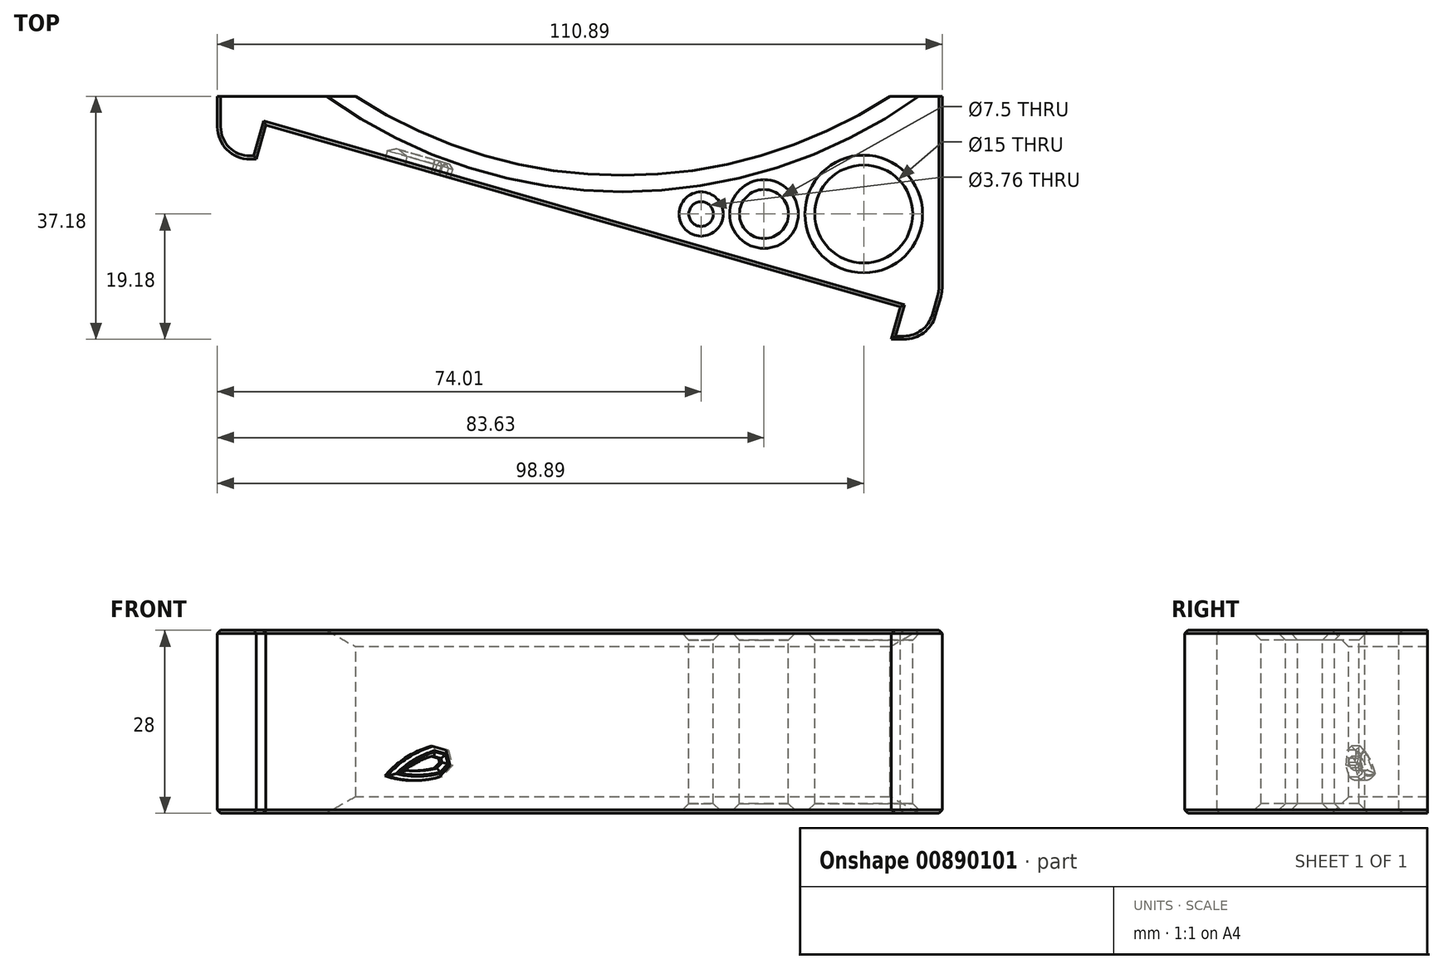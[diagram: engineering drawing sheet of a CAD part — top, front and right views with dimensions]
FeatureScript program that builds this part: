
annotation { "Feature Type Name" : "Feature", "Feature Type Description" : "" }
export const myFeature = defineFeature(function(context is Context, id is Id, definition is map)
    precondition{}
    {
        {
            var Q0;
            Q0=qCreatedBy(makeId("Front.planeOp"),FACE);
            var sketch = newSketch(context, id + "F0", { "sketchPlane" : qUnion([Q0])});
            skLineSegment(sketch, "E0", {"start": v(-54.27, 0) * mm, "end": v(46.5, 0) * mm, "construction": true});
            skLineSegment(sketch, "E1", {"start": v(-54.27, 0) * mm, "end": v(41.86, 27.56) * mm});
            skLineSegment(sketch, "E2", {"start": v(-54.27, 0) * mm, "end": v(-57.03, 9.61) * mm});
            skLineSegment(sketch, "E3", {"start": v(-57.03, 9.61) * mm, "end": v(39.1, 37.18) * mm});
            skLineSegment(sketch, "E4", {"start": v(39.1, 37.18) * mm, "end": v(41.86, 27.56) * mm});
            skSolve(sketch);
        }
        {
            var Q0;
            Q0=makeQuery(id+"F0.imprint","IMPRINT",FACE,{"disambiguationData":[TD([[makeQuery(id+"F0.imprint","IMPRINT",EDGE,{"derivedFrom":sQuery(id+"F0.wireOp",EDGE,"E1")}),1.0]])]});
            extrude(context, id + "F1", {"entities" : qUnion([Q0]), "depth" : 26 * mm, "offsetDistance" : 25 * mm, "symmetric" : true});
        }
        {
            var Q0;
            Q0=qCreatedBy(makeId("Front.planeOp"),FACE);
            var sketch = newSketch(context, id + "F2", { "sketchPlane" : qUnion([Q0])});
            skLineSegment(sketch, "E5.0", {"start": v(-54.61, -0.62) * mm, "end": v(-56.11, 4.61) * mm});
            skLineSegment(sketch, "E5.1", {"start": v(-54.61, -0.62) * mm, "end": v(42.47, 27.22) * mm});
            skLineSegment(sketch, "E5.2", {"start": v(41.05, 32.18) * mm, "end": v(42.47, 27.22) * mm});
            skLineSegment(sketch, "E6", {"start": v(41.05, 32.18) * mm, "end": v(46.77, 32.18) * mm});
            skLineSegment(sketch, "E7", {"start": v(48.86, 24.92) * mm, "end": v(48.86, -5) * mm});
            skLineSegment(sketch, "E8", {"start": v(-56.11, 4.61) * mm, "end": v(-62.03, 4.61) * mm});
            skLineSegment(sketch, "E9", {"start": v(-62.03, 4.61) * mm, "end": v(-62.03, -5) * mm});
            skLineSegment(sketch, "E10", {"start": v(-62.03, -5) * mm, "end": v(-40.86, -5) * mm});
            skLineSegment(sketch, "E11", {"start": v(48.86, 24.92) * mm, "end": v(46.77, 32.18) * mm});
            skArc(sketch, "E12", {"start": v(40.86, -5) * mm, "mid": v(0, 7.1) * mm, "end": v(-40.86, -5) * mm});
            skLineSegment(sketch, "E13.trimOffspring", {"start": v(40.86, -5) * mm, "end": v(48.86, -5) * mm});
            skCircle(sketch, "E14", {"center": v(36.86, 13) * mm, "radius": 7.5 * mm});
            skCircle(sketch, "E15", {"center": v(21.6, 13) * mm, "radius": 3.75 * mm});
            skCircle(sketch, "E16", {"center": v(11.98, 13) * mm, "radius": 1.88 * mm});
            skLineSegment(sketch, "E17", {"start": v(-40.86, -5) * mm, "end": v(40.86, -5) * mm, "construction": true});
            skSolve(sketch);
        }
        {
            var Q0;
            Q0=makeQuery(id+"F2.imprint","IMPRINT",FACE,{"disambiguationData":[TD([[makeQuery(id+"F2.imprint","IMPRINT",EDGE,{"derivedFrom":sQuery(id+"F2.wireOp",EDGE,"E5.0")}),1.0]])]});
            extrude(context, id + "F3", {"entities" : qUnion([Q0]), "depth" : 28 * mm, "offsetDistance" : 25 * mm, "symmetric" : true});
        }
        {
            var Q0;
            Q0=makeQuery(id+"F3.opExtrude","CAP_EDGE",EDGE,{"disambiguationData":[OSD([sQuery(id+"F2.wireOp",EDGE,"E12")])],"isStart":false});
            var Q1;
            Q1=makeQuery(id+"F3.opExtrude","CAP_EDGE",EDGE,{"disambiguationData":[OSD([sQuery(id+"F2.wireOp",EDGE,"E12")])],"isStart":true});
            chamfer(context, id + "F4", {"entities" : qUnion([Q0, Q1]), "width" : 2.5 * mm, "tangentPropagation" : true});
        }
        {
            var Q0;
            Q0=makeQuery(id+"F3.opExtrude","SWEPT_EDGE",EDGE,{"disambiguationData":[OSD([sQuery(id+"F2.wireOp",EDGE,"E8"),sQuery(id+"F2.wireOp",EDGE,"E9")])]});
            var Q1;
            Q1=makeQuery(id+"F3.opExtrude","SWEPT_EDGE",EDGE,{"disambiguationData":[OSD([sQuery(id+"F2.wireOp",EDGE,"E6"),sQuery(id+"F2.wireOp",EDGE,"E11")])]});
            var Q2;
            Q2=makeQuery(id+"F3.opExtrude","SWEPT_EDGE",EDGE,{"disambiguationData":[OSD([sQuery(id+"F2.wireOp",EDGE,"E7"),sQuery(id+"F2.wireOp",EDGE,"E11")])]});
            fillet(context, id + "F5", {"entities" : qUnion([Q0, Q1, Q2]), "radius" : 5 * mm, "tangentPropagation" : true, "allowEdgeOverflow" : false});
        }
        {
            var Q0;
            Q0=makeQuery(id+"F3.opExtrude","SWEPT_FACE",FACE,{"disambiguationData":[OSD([sQuery(id+"F2.wireOp",EDGE,"E15")])]});
            var Q1;
            Q1=makeQuery(id+"F3.opExtrude","SWEPT_FACE",FACE,{"disambiguationData":[OSD([sQuery(id+"F2.wireOp",EDGE,"E14")])]});
            var Q2;
            Q2=makeQuery(id+"F3.opExtrude","SWEPT_FACE",FACE,{"disambiguationData":[OSD([sQuery(id+"F2.wireOp",EDGE,"E16")])]});
            chamfer(context, id + "F6", {"entities" : qUnion([Q0, Q1, Q2]), "width" : 1.5 * mm, "tangentPropagation" : true});
        }
        {
            var Q0;
            Q0=makeQuery(id+"F3.opExtrude","CAP_EDGE",EDGE,{"disambiguationData":[OSD([sQuery(id+"F2.wireOp",EDGE,"E7")])],"isStart":false});
            var Q1;
            Q1=makeQuery(id+"F3.opExtrude","CAP_EDGE",EDGE,{"disambiguationData":[OSD([sQuery(id+"F2.wireOp",EDGE,"E7")])],"isStart":true});
            var Q2;
            Q2=makeQuery(id+"F3.opExtrude","CAP_EDGE",EDGE,{"disambiguationData":[OSD([sQuery(id+"F2.wireOp",EDGE,"E5.1")])],"isStart":false});
            var Q3;
            Q3=makeQuery(id+"F3.opExtrude","CAP_EDGE",EDGE,{"disambiguationData":[OSD([sQuery(id+"F2.wireOp",EDGE,"E5.2")])],"isStart":false});
            var Q4;
            Q4=makeQuery(id+"F3.opExtrude","CAP_EDGE",EDGE,{"disambiguationData":[OSD([sQuery(id+"F2.wireOp",EDGE,"E9")])],"isStart":false});
            var Q5;
            Q5=makeQuery(id+"F3.opExtrude","CAP_EDGE",EDGE,{"disambiguationData":[OSD([sQuery(id+"F2.wireOp",EDGE,"E5.0")])],"isStart":false});
            var Q6;
            Q6=makeQuery(id+"F3.opExtrude","CAP_EDGE",EDGE,{"disambiguationData":[OSD([sQuery(id+"F2.wireOp",EDGE,"E8")])],"isStart":false});
            var Q7;
            Q7=makeQuery(id+"F3.opExtrude","CAP_EDGE",EDGE,{"disambiguationData":[OSD([sQuery(id+"F2.wireOp",EDGE,"E5.0")])],"isStart":true});
            var Q8;
            Q8=makeQuery(id+"F3.opExtrude","CAP_EDGE",EDGE,{"disambiguationData":[OSD([sQuery(id+"F2.wireOp",EDGE,"E8")])],"isStart":true});
            var Q9;
            Q9=makeQuery(id+"F3.opExtrude","CAP_EDGE",EDGE,{"disambiguationData":[OSD([sQuery(id+"F2.wireOp",EDGE,"E9")])],"isStart":true});
            var Q10;
            Q10=makeQuery(id+"F3.opExtrude","CAP_EDGE",EDGE,{"disambiguationData":[OSD([sQuery(id+"F2.wireOp",EDGE,"E5.1")])],"isStart":true});
            var Q11;
            Q11=makeQuery(id+"F3.opExtrude","CAP_EDGE",EDGE,{"disambiguationData":[OSD([sQuery(id+"F2.wireOp",EDGE,"E5.2")])],"isStart":true});
            chamfer(context, id + "F7", {"entities" : qUnion([Q0, Q1, Q2, Q3, Q4, Q5, Q6, Q7, Q8, Q9, Q10, Q11]), "width" : .5 * mm, "tangentPropagation" : true});
        }
        {
            var Q0;
            Q0=makeQuery(id+"F3.opExtrude","SWEPT_FACE",FACE,{"disambiguationData":[OSD([sQuery(id+"F2.wireOp",EDGE,"E5.1")])]});
            var sketch = newSketch(context, id + "F8", { "sketchPlane" : qUnion([Q0])});
            skLineSegment(sketch, "E18", {"start": v(-23.34, -6.71) * mm, "end": v(-25.06, -8.45) * mm});
            skArc(sketch, "E19", {"start": v(24.14, 7.53) * mm, "mid": v(16.84, 8.62) * mm, "end": v(9.47, 8.9) * mm});
            skLineSegment(sketch, "E20", {"start": v(-23.98, -4.35) * mm, "end": v(-23.34, -6.71) * mm});
            skArc(sketch, "E21", {"start": v(3.32, 8.49) * mm, "mid": v(-11.3, 5.13) * mm, "end": v(-24.78, -1.44) * mm});
            skArc(sketch, "E22", {"start": v(-26.35, -3.73) * mm, "mid": v(-30.37, -5.47) * mm, "end": v(-33.74, -8.29) * mm});
            skArc(sketch, "E23", {"start": v(-33.74, -8.29) * mm, "mid": v(-29.41, -9) * mm, "end": v(-25.06, -8.45) * mm});
            skLineSegment(sketch, "E24", {"start": v(-26.35, -3.73) * mm, "end": v(-23.98, -4.35) * mm});
            skEllipticalArc(sketch, "E25", {});
            skArc(sketch, "E26", {"start": v(-22.54, -9.63) * mm, "mid": v(-20.46, -4.66) * mm, "end": v(-24.78, -1.44) * mm});
            skArc(sketch, "E27", {"start": v(-22.54, -9.63) * mm, "mid": v(2.47, -5.6) * mm, "end": v(24.14, 7.53) * mm});
            skLineSegment(sketch, "E28", {"start": v(-33.74, -8.29) * mm, "end": v(24.14, 7.53) * mm, "construction": true});
            skPoint(sketch, "E29", {"position": v(-4.8, -0.38) * mm});
            skArc(sketch, "E30.0", {"start": v(-30.58, -7.42) * mm, "mid": v(-28.2, -7.47) * mm, "end": v(-25.83, -7.1) * mm});
            skArc(sketch, "E30.1", {"start": v(-26.33, -5.28) * mm, "mid": v(-28.55, -6.17) * mm, "end": v(-30.58, -7.42) * mm});
            skLineSegment(sketch, "E30.2", {"start": v(-25, -6.27) * mm, "end": v(-25.83, -7.1) * mm});
            skLineSegment(sketch, "E30.3", {"start": v(-25.2, -5.58) * mm, "end": v(-25, -6.27) * mm});
            skLineSegment(sketch, "E30.4", {"start": v(-26.33, -5.28) * mm, "end": v(-25.2, -5.58) * mm});
            skArc(sketch, "E31.0", {"start": v(-19.28, -8.15) * mm, "mid": v(-19, -4.26) * mm, "end": v(-21.22, -1.06) * mm});
            skArc(sketch, "E31.1", {"start": v(0.46, 6.58) * mm, "mid": v(-10.72, 3.73) * mm, "end": v(-21.22, -1.06) * mm});
            skArc(sketch, "E31.2", {"start": v(-19.28, -8.15) * mm, "mid": v(2, -4.17) * mm, "end": v(20.78, 6.61) * mm});
            skArc(sketch, "E31.3", {"start": v(20.78, 6.61) * mm, "mid": v(16.69, 7.12) * mm, "end": v(12.58, 7.37) * mm});
            skFitSpline(sketch, "E31.4", {"points": [v(2.46, 9.73) * mm, v(2.03, 9.43) * mm, v(1.24, 8.73) * mm, v(0.6, 7.56) * mm, v(0.43, 6.51) * mm, v(0.47, 5.7) * mm, v(0.7, 4.94) * mm, v(1.09, 4.25) * mm, v(1.6, 3.65) * mm, v(2.2, 3.15) * mm, v(2.87, 2.73) * mm, v(3.6, 2.41) * mm, v(4.39, 2.17) * mm, v(5.2, 2.02) * mm, v(6.03, 1.95) * mm, v(6.87, 1.97) * mm, v(7.7, 2.06) * mm, v(8.52, 2.24) * mm, v(9.31, 2.5) * mm, v(10.05, 2.84) * mm, v(10.73, 3.25) * mm, v(11.35, 3.75) * mm, v(11.87, 4.33) * mm, v(12.29, 5) * mm, v(12.57, 5.74) * mm, v(12.69, 6.53) * mm, v(12.62, 7.34) * mm, v(12.28, 8.35) * mm, v(11.49, 9.42) * mm, v(10.62, 10) * mm, v(10.14, 10.24) * mm]});
            const initialGuessF8  = {"E25": [0.006554140104909864, 0.00647352985779553, 0.9982026826847827, 0.05992832619807634, 0.004600005458673202, 0.002995510400761797, 2.313906, 0.8451846928204213]};
            skSetInitialGuess(sketch, initialGuessF8);
            skSolve(sketch);
        }
        {
            var Q0;
            {var subQ1=sQuery(id+"F2.wireOp",EDGE,"E5.1");var subQ2=sQuery(id+"F2.wireOp",EDGE,"E5.0");Q0=makeQuery(id+"F10.boolean.opBoolean","SPLIT",FACE,{"disambiguationData":[TD([makeQuery(id+"F3.opExtrude","SWEPT_FACE",FACE,{"disambiguationData":[OSD([subQ2])]})])],"derivedFrom":makeQuery(id+"F3.opExtrude","SWEPT_FACE",FACE,{"disambiguationData":[OSD([subQ1])]})});}
            var sketch = newSketch(context, id + "F9", { "sketchPlane" : qUnion([Q0])});
            skArc(sketch, "E32.0.0", {"start": v(-24.78, -1.44) * mm, "mid": v(-20.46, -4.66) * mm, "end": v(-22.54, -9.63) * mm});
            skArc(sketch, "E32.0.1", {"start": v(-22.54, -9.63) * mm, "mid": v(2.47, -5.6) * mm, "end": v(24.14, 7.53) * mm});
            skArc(sketch, "E32.0.2", {"start": v(24.14, 7.53) * mm, "mid": v(16.84, 8.62) * mm, "end": v(9.47, 8.9) * mm});
            skEllipticalArc(sketch, "E32.0.3", {});
            skArc(sketch, "E32.0.4", {"start": v(3.32, 8.49) * mm, "mid": v(-11.3, 5.13) * mm, "end": v(-24.78, -1.44) * mm});
            skArc(sketch, "E33.0", {"start": v(-26.35, -3.73) * mm, "mid": v(-30.37, -5.47) * mm, "end": v(-33.74, -8.29) * mm});
            skLineSegment(sketch, "E34.0.0", {"start": v(-25.2, -5.58) * mm, "end": v(-26.33, -5.28) * mm});
            skArc(sketch, "E34.0.1", {"start": v(-26.33, -5.28) * mm, "mid": v(-28.55, -6.17) * mm, "end": v(-30.58, -7.42) * mm});
            skArc(sketch, "E34.0.2", {"start": v(-30.58, -7.42) * mm, "mid": v(-28.2, -7.47) * mm, "end": v(-25.83, -7.1) * mm});
            skLineSegment(sketch, "E34.0.3", {"start": v(-25.83, -7.1) * mm, "end": v(-25, -6.27) * mm});
            skLineSegment(sketch, "E34.0.4", {"start": v(-25, -6.27) * mm, "end": v(-25.2, -5.58) * mm});
            skLineSegment(sketch, "E35.0.0", {"start": v(-23.98, -4.35) * mm, "end": v(-26.35, -3.73) * mm});
            skArc(sketch, "E35.0.2", {"start": v(-33.74, -8.29) * mm, "mid": v(-29.41, -9) * mm, "end": v(-25.06, -8.45) * mm});
            skLineSegment(sketch, "E35.0.3", {"start": v(-25.06, -8.45) * mm, "end": v(-23.34, -6.71) * mm});
            skLineSegment(sketch, "E35.0.4", {"start": v(-23.34, -6.71) * mm, "end": v(-23.98, -4.35) * mm});
            skFitSpline(sketch, "E36", {"points": [v(-21.22, -1.06) * mm, v(-10.72, 3.73) * mm, v(0.46, 6.58) * mm], "startDerivative": vector(17.1, 9.18) * mm, "endDerivative": vector(20.13, 3.79) * mm});
            skFitSpline(sketch, "E37", {"points": [v(0.46, 6.58) * mm, v(1.77, 3.5) * mm, v(6.86, 1.98) * mm, v(11.31, 3.75) * mm, v(12.58, 7.37) * mm], "startDerivative": vector(3.02, -20.54) * mm, "endDerivative": vector(-3.52, 19.16) * mm});
            skFitSpline(sketch, "E38", {"points": [v(12.58, 7.37) * mm, v(16.69, 7.12) * mm, v(20.78, 6.61) * mm], "startDerivative": vector(6.88, -0.26) * mm, "endDerivative": vector(8.62, -1.26) * mm});
            skPoint(sketch, "E39.0", {"position": v(-19.28, -8.15) * mm});
            skPoint(sketch, "E40.0", {"position": v(2, -4.17) * mm});
            skPoint(sketch, "E41.0", {"position": v(-19, -4.26) * mm});
            skFitSpline(sketch, "E42", {"points": [v(20.78, 6.61) * mm, v(2, -4.17) * mm, v(-7.83, -6.93) * mm, v(-19.28, -8.15) * mm], "startDerivative": vector(-35.3, -32.24) * mm, "endDerivative": vector(-8.5, 0.33) * mm});
            skFitSpline(sketch, "E43", {"points": [v(-21.22, -1.06) * mm, v(-19, -4.26) * mm, v(-19.28, -8.15) * mm], "startDerivative": vector(8.05, -5.42) * mm, "endDerivative": vector(-3.64, -8.61) * mm});
            const initialGuessF9  = {"E32.0.3": [0.00655414012856891, 0.0064735298560076576, 0.9982026826847827, 0.059928326198076316, 0.004600005458673202, 0.002995510400761797, 2.313906, 0.8451842568515852]};
            skSetInitialGuess(sketch, initialGuessF9);
            skSolve(sketch);
        }
        {
            var Q0;
            Q0=makeQuery(id+"F9.imprint","IMPRINT",FACE,{"disambiguationData":[TD([[makeQuery(id+"F9.imprint","IMPRINT",EDGE,{"derivedFrom":sQuery(id+"F9.wireOp",EDGE,"E32.0.0")}),1.0]])]});
            var Q1;
            Q1=makeQuery(id+"F9.imprint","IMPRINT",FACE,{"disambiguationData":[TD([[makeQuery(id+"F9.imprint","IMPRINT",EDGE,{"derivedFrom":sQuery(id+"F9.wireOp",EDGE,"E34.0.0")}),-1.0]])]});
            extrude(context, id + "F10", {"entities" : qUnion([Q0, Q1]), "operationType" : NewBodyOperationType.REMOVE, "oppositeDirection" : true, "depth" : 2 * mm, "offsetDistance" : 25 * mm});
        }
        {
            var Q0;
            Q0=makeQuery(id+"F10.boolean.opBoolean","COPY",FACE,{"derivedFrom":makeQuery(id+"F10.opExtrude","CAP_FACE",FACE,{"disambiguationData":[OSD([sQuery(id+"F9.wireOp",EDGE,"E32.0.0"),sQuery(id+"F9.wireOp",EDGE,"E32.0.1"),sQuery(id+"F9.wireOp",EDGE,"E32.0.2"),sQuery(id+"F9.wireOp",EDGE,"E32.0.3"),sQuery(id+"F9.wireOp",EDGE,"E32.0.4"),sQuery(id+"F9.wireOp",EDGE,"E36"),sQuery(id+"F9.wireOp",EDGE,"E37"),sQuery(id+"F9.wireOp",EDGE,"E38"),sQuery(id+"F9.wireOp",EDGE,"E42"),sQuery(id+"F9.wireOp",EDGE,"E43")])],"isStart":false})});
            var Q1;
            Q1=makeQuery(id+"F10.boolean.opBoolean","COPY",FACE,{"derivedFrom":makeQuery(id+"F10.opExtrude","CAP_FACE",FACE,{"disambiguationData":[OSD([sQuery(id+"F9.wireOp",EDGE,"E34.0.0"),sQuery(id+"F9.wireOp",EDGE,"E34.0.1"),sQuery(id+"F9.wireOp",EDGE,"E34.0.2"),sQuery(id+"F9.wireOp",EDGE,"E34.0.3"),sQuery(id+"F9.wireOp",EDGE,"E34.0.4"),sQuery(id+"F9.wireOp",EDGE,"E35.0.0"),sQuery(id+"F9.wireOp",EDGE,"E33.0"),sQuery(id+"F9.wireOp",EDGE,"E35.0.2"),sQuery(id+"F9.wireOp",EDGE,"E35.0.3"),sQuery(id+"F9.wireOp",EDGE,"E35.0.4")])],"isStart":false})});
            chamfer(context, id + "F11", {"entities" : qUnion([Q0, Q1]), "width" : .65 * mm, "tangentPropagation" : true});
        }
        {
            var Q0;
            Q0=makeQuery(id+"F1.opExtrude","SWEPT_BODY",BODY,{"disambiguationData":[OSD([sQuery(id+"F0.wireOp",EDGE,"E1"),sQuery(id+"F0.wireOp",EDGE,"E2"),sQuery(id+"F0.wireOp",EDGE,"E3"),sQuery(id+"F0.wireOp",EDGE,"E4")])]});
            deleteBodies(context, id + "F12", {"entities" : qUnion([Q0])});
        }
        {
            var Q0;
            Q0=makeQuery(id+"F3.opExtrude","SWEPT_BODY",BODY,{"disambiguationData":[OSD([sQuery(id+"F2.wireOp",EDGE,"E5.0"),sQuery(id+"F2.wireOp",EDGE,"E5.1"),sQuery(id+"F2.wireOp",EDGE,"E5.2"),sQuery(id+"F2.wireOp",EDGE,"E6"),sQuery(id+"F2.wireOp",EDGE,"E7"),sQuery(id+"F2.wireOp",EDGE,"E8"),sQuery(id+"F2.wireOp",EDGE,"E9"),sQuery(id+"F2.wireOp",EDGE,"E10"),sQuery(id+"F2.wireOp",EDGE,"E11"),sQuery(id+"F2.wireOp",EDGE,"E12"),sQuery(id+"F2.wireOp",EDGE,"E13.trimOffspring"),sQuery(id+"F2.wireOp",EDGE,"E14"),sQuery(id+"F2.wireOp",EDGE,"E15"),sQuery(id+"F2.wireOp",EDGE,"E16")])]});
            var Q1;
            Q1=makeQuery(id+"F3.opExtrude","CAP_EDGE",EDGE,{"disambiguationData":[OSD([sQuery(id+"F2.wireOp",EDGE,"E10")])],"isStart":false});
            transform(context, id + "F13", {"entities" : qUnion([Q0]), "transformType" : TransformType.ROTATION, "transformAxis" : qUnion([Q1]), "angle" : 90 * degree, "makeCopy" : false});
        }
        {
            var Q0;
            Q0=makeQuery(id+"F3.opExtrude","SWEPT_FACE",FACE,{"disambiguationData":[OSD([sQuery(id+"F2.wireOp",EDGE,"E10")])]});
            cPlane(context, id + "F14", {"entities" : qUnion([Q0]), "cplaneType" : CPlaneType.OFFSET, "offset" : 0 * mm, "width" : 150 * mm, "height" : 150 * mm});
        }
    });
